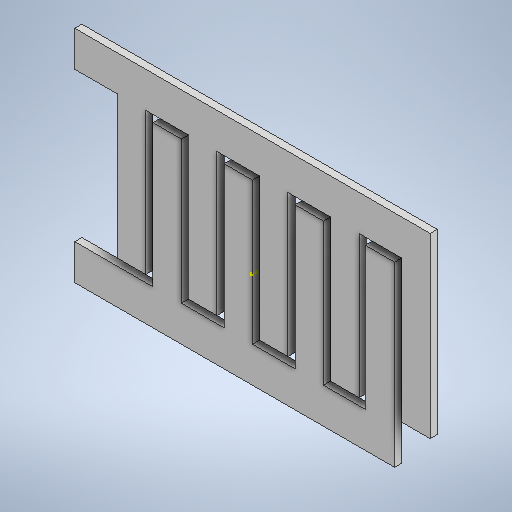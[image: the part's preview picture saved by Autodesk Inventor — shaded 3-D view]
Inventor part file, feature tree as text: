
AUTODESK INVENTOR PART (.ipt)
format: ipt  version: 2025.2 (Build 292293000, 293)  size: 614,912 bytes
history: native  units: in
note: dims shown in document units (in); Inventor stores cm internally (conversion verified against a paired STEP export)
features: sketch x4, extrude x1
ambient origin geometry x8: Origin, YZ Plane, XZ Plane, XY Plane, X Axis, Y Axis, Z Axis, Center Point
bodies: Solid1 (feature_tree)
feature tree (5):
  sketch  "Sketch1"  dims[d8=1.9685in d11=0.1969in]
  sketch  "Sketch2"  dims[d13=0.1575in]
  sketch  "Sketch3"  dims[d14=0.9843in]
  extrude  "Extrusion1"  Depth=0.1969in
  sketch  "Sketch4"  dims[d16=0.2362in d27=0.2362in d28=0.2362in d29=0.2362in d30=0.2362in d48=0.1969in d49=0.0394in d50=0.0in]
